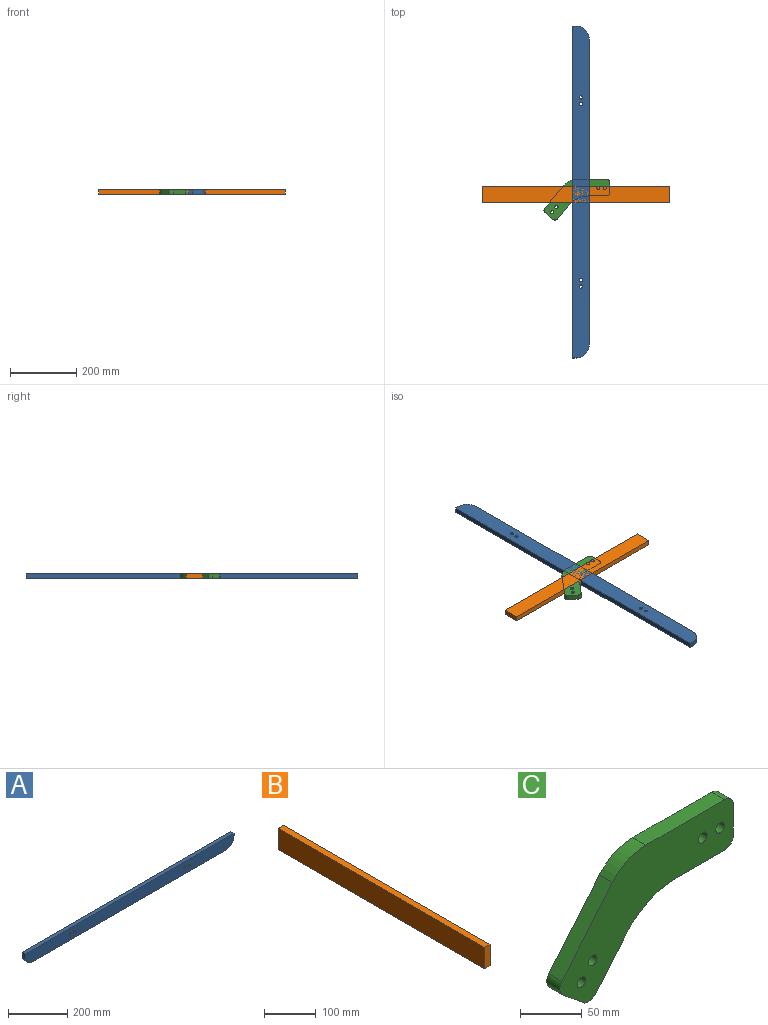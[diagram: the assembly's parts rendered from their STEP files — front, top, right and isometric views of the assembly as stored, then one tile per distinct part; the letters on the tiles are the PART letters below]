
ASSEMBLY  parts=3 mates=1
PART A: 12 faces, bbox 1000x15x50 mm
  f0: cylinder r=40mm len=40mm, axis (0,1,0), area 942.5mm2, adj f1,f5,f6,f7
  f1: plane 920x15mm, normal (0,0,-1), area 13800mm2, adj f0,f2,f6,f7
  f2: cylinder r=40mm len=40mm, axis (0,1,0), area 942.5mm2, adj f1,f3,f6,f7
  f3: plane 15x10mm, normal (1,0,0), area 150mm2, adj f2,f4,f6,f7
  f4: plane 1000x15mm, normal (0,0,1), area 15000mm2, adj f3,f5,f6,f7
  f5: plane 15x10mm, normal (-1,0,0), area 150mm2, adj f0,f4,f6,f7
  f6: plane 1000x50mm, normal (0,-1,0), area 48999.1mm2, adj f0,f1,f2,f3,f4,f5,f8,f9
  f7: plane 1000x50mm, normal (0,1,0), area 48999.1mm2, adj f0,f1,f2,f3,f4,f5,f8,f9
  f8: cylinder r=5mm len=15mm, axis (0,1,0), area 471.2mm2, adj f6,f7
  f9: cylinder r=5mm len=15mm, axis (0,1,0), area 471.2mm2, adj f6,f7
  f10: cylinder r=5mm len=15mm, axis (0,1,0), area 471.2mm2, adj f6,f7
  f11: cylinder r=5mm len=15mm, axis (0,1,0), area 471.2mm2, adj f6,f7
PART B: 6 faces, bbox 15x562.5x50 mm
  f0: plane 50x15mm, normal (0,-1,0), area 750mm2, adj f1,f2,f3,f4
  f1: plane 562.5x50mm, normal (-1,0,0), area 28125mm2, adj f0,f2,f4,f5
  f2: plane 562.5x15mm, normal (0,0,-1), area 8437.5mm2, adj f0,f1,f3,f5
  f3: plane 562.5x50mm, normal (1,0,0), area 28125mm2, adj f0,f2,f4,f5
  f4: plane 562.5x15mm, normal (0,0,1), area 8437.5mm2, adj f0,f1,f3,f5
  f5: plane 50x15mm, normal (0,1,0), area 750mm2, adj f1,f2,f3,f4
PART C: 18 faces, bbox 198.5x15x122.5 mm
  f0: plane 22.98x19.28mm, normal (-0.64,0,-0.77), area 450mm2, adj f1,f11,f12,f13
  f1: cylinder r=10mm len=15mm, axis (0,-1,0), area 235.6mm2, adj f0,f2,f12,f13
  f2: plane 42.15x35.37mm, normal (0.77,0,-0.64), area 825.4mm2, adj f1,f3,f12,f13
  f3: cylinder r=75mm len=57.45mm, axis (0,-1,0), area 981.7mm2, adj f2,f4,f12,f13
  f4: plane 55.03x15mm, normal (0,0,-1), area 825.4mm2, adj f3,f5,f12,f13
  f5: cylinder r=10mm len=15mm, axis (0,-1,0), area 235.6mm2, adj f4,f6,f12,f13
  f6: plane 30x15mm, normal (1,0,0), area 450mm2, adj f5,f7,f12,f13
  f7: cylinder r=10mm len=15mm, axis (0,-1,0), area 235.6mm2, adj f6,f8,f12,f13
  f8: plane 90x15mm, normal (0,0,1), area 1350mm2, adj f7,f9,f12,f13
  f9: cylinder r=50mm len=38.3mm, axis (0,-1,0), area 654.5mm2, adj f8,f10,f12,f13
  f10: plane 68.94x57.85mm, normal (-0.77,0,0.64), area 1350mm2, adj f9,f11,f12,f13
  f11: cylinder r=10mm len=15mm, axis (0,-1,0), area 235.6mm2, adj f0,f10,f12,f13
  f12: plane 198.49x122.52mm, normal (0,1,0), area 10859.4mm2, adj f0,f1,f2,f3,f4,f5,f6,f7
  f13: plane 198.49x122.52mm, normal (0,-1,0), area 10859.4mm2, adj f0,f1,f2,f3,f4,f5,f6,f7
  f14: cylinder r=5mm len=15mm, axis (0,1,0), area 471.2mm2, adj f12,f13
  f15: cylinder r=5mm len=15mm, axis (0,1,0), area 471.2mm2, adj f12,f13
  f16: cylinder r=5mm len=15mm, axis (0,1,0), area 471.2mm2, adj f12,f13
  f17: cylinder r=5mm len=15mm, axis (0,1,0), area 471.2mm2, adj f12,f13
PLACE A rot(axis=(-0.58,-0.58,0.58),120deg) t=(-737.66,7.5,168.64)mm
PLACE B rot(axis=(0.58,0.58,-0.58),120deg) t=(-727.66,-25,24.89)mm
PLACE C rot(axis=(-1,0,0),90deg) t=(-375.57,45.5,183.64)mm
MATE fastened B.f1 <-> C.f13  axis (0,0,1) through (-727.66,0,464.89)mm
